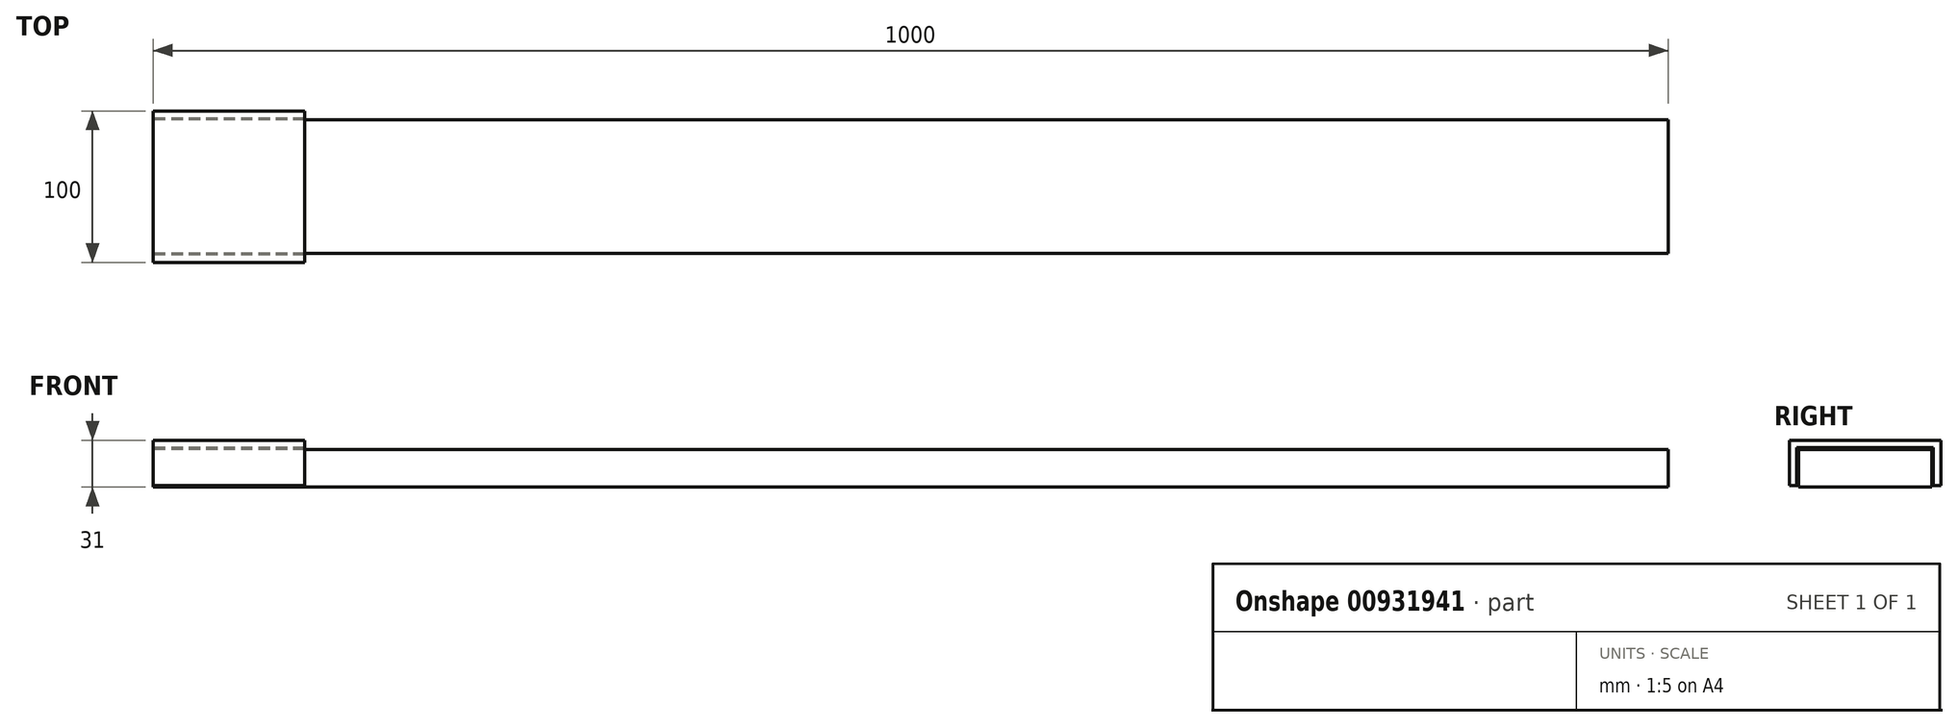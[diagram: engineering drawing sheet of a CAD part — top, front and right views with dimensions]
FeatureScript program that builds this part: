
annotation { "Feature Type Name" : "Feature", "Feature Type Description" : "" }
export const myFeature = defineFeature(function(context is Context, id is Id, definition is map)
    precondition{}
    {
        {
            var Q0;
            Q0=qCreatedBy(makeId("Right.planeOp"),FACE);
            var sketch = newSketch(context, id + "F0", { "sketchPlane" : qUnion([Q0])});
            skLineSegment(sketch, "E0", {"start": v(50, 0) * mm, "end": v(-50, 0) * mm});
            skLineSegment(sketch, "E1", {"start": v(-50, 0) * mm, "end": v(-50, -30) * mm});
            skLineSegment(sketch, "E2", {"start": v(-50, -30) * mm, "end": v(-45, -30) * mm});
            skLineSegment(sketch, "E3", {"start": v(-45, -30) * mm, "end": v(-45, -5) * mm});
            skLineSegment(sketch, "E4", {"start": v(-45, -5) * mm, "end": v(45, -5) * mm});
            skLineSegment(sketch, "E5", {"start": v(45, -5) * mm, "end": v(45, -30) * mm});
            skLineSegment(sketch, "E6", {"start": v(45, -30) * mm, "end": v(50, -30) * mm});
            skLineSegment(sketch, "E7", {"start": v(50, -30) * mm, "end": v(50, 0) * mm});
            skSolve(sketch);
        }
        {
            var Q0;
            Q0 = qSketchRegion(id + "F0", true);
            extrude(context, id + "F1", {"entities" : qUnion([Q0]), "depth" : 100 * mm, "offsetDistance" : 25 * mm});
        }
        {
            var Q0;
            Q0=qCreatedBy(makeId("Right.planeOp"),FACE);
            var sketch = newSketch(context, id + "F2", { "sketchPlane" : qUnion([Q0])});
            skLineSegment(sketch, "E8.bottom", {"start": v(-44, -6) * mm, "end": v(44, -6) * mm});
            skLineSegment(sketch, "E8.top", {"start": v(-44, -31) * mm, "end": v(44, -31) * mm});
            skLineSegment(sketch, "E8.left", {"start": v(-44, -6) * mm, "end": v(-44, -31) * mm});
            skLineSegment(sketch, "E8.right", {"start": v(44, -6) * mm, "end": v(44, -31) * mm});
            skLineSegment(sketch, "E9.bottom", {"start": v(44, -31) * mm, "end": v(44, -31) * mm});
            skLineSegment(sketch, "E9.top", {"start": v(44, -32.05) * mm, "end": v(44, -32.05) * mm});
            skLineSegment(sketch, "E9.left", {"start": v(44, -32.05) * mm, "end": v(44, -31) * mm});
            skLineSegment(sketch, "E9.right", {"start": v(44, -32.05) * mm, "end": v(44, -31) * mm});
            skSolve(sketch);
        }
        {
            var Q0;
            Q0 = qSketchRegion(id + "F2", true);
            extrude(context, id + "F3", {"entities" : qUnion([Q0]), "depth" : 1000 * mm, "offsetDistance" : 25 * mm});
        }
    });
